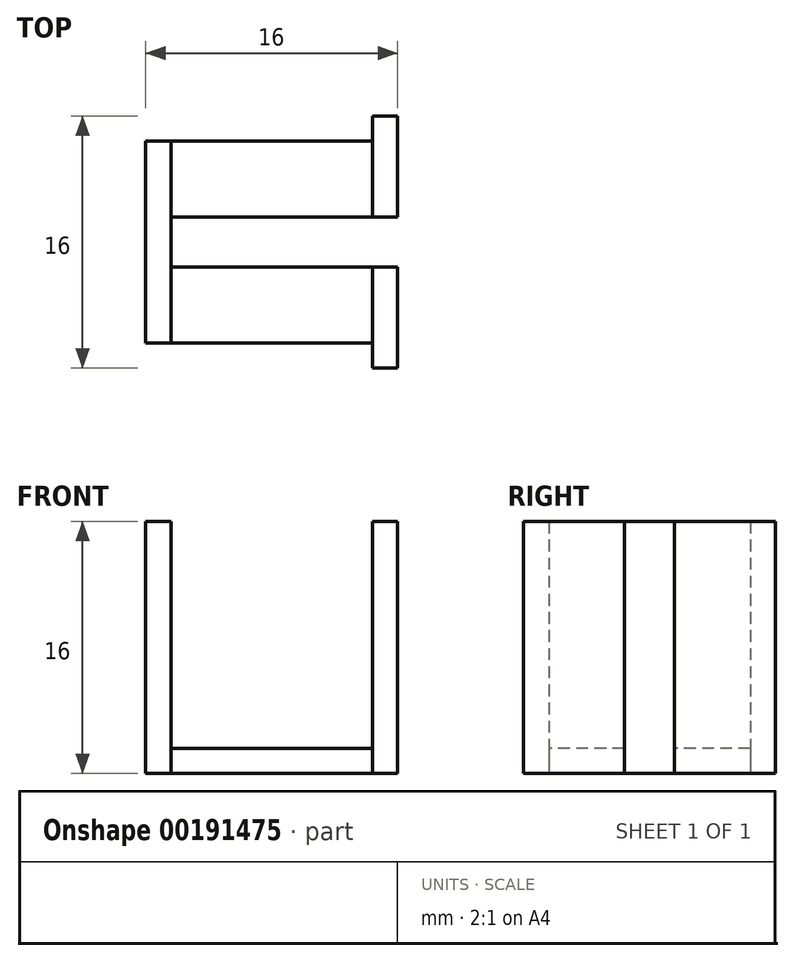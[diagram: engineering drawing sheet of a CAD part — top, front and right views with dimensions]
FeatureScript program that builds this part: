
annotation { "Feature Type Name" : "Feature", "Feature Type Description" : "" }
export const myFeature = defineFeature(function(context is Context, id is Id, definition is map)
    precondition{}
    {
        {
            assignVariable(context, id + "F0", {"name" : "FLU", "anyValue" : 1.6});
        }
        {
            var Q0;
            Q0=qCreatedBy(makeId("Top.planeOp"),FACE);
            var sketch = newSketch(context, id + "F1", { "sketchPlane" : qUnion([Q0])});
            skLineSegment(sketch, "E0.bottom", {"start": v(8, 8) * mm, "end": v(-8, 8) * mm});
            skLineSegment(sketch, "E0.top", {"start": v(8, -8) * mm, "end": v(-8, -8) * mm});
            skLineSegment(sketch, "E0.left", {"start": v(8, 8) * mm, "end": v(8, -8) * mm});
            skLineSegment(sketch, "E0.right", {"start": v(-8, 8) * mm, "end": v(-8, -8) * mm});
            skPoint(sketch, "E0.middle", {"position": v(0, 0) * mm});
            skLineSegment(sketch, "E1", {"start": v(-6.4, 8) * mm, "end": v(-6.4, -8) * mm});
            skLineSegment(sketch, "E2", {"start": v(6.4, 8) * mm, "end": v(6.4, -8) * mm});
            skLineSegment(sketch, "E3", {"start": v(-8, 6.4) * mm, "end": v(8, 6.4) * mm});
            skLineSegment(sketch, "E4", {"start": v(-8, -6.4) * mm, "end": v(8.33, -6.4) * mm});
            skLineSegment(sketch, "E5", {"start": v(-8, 1.6) * mm, "end": v(8, 1.6) * mm});
            skLineSegment(sketch, "E6", {"start": v(-8, -1.6) * mm, "end": v(8, -1.6) * mm});
            skSolve(sketch);
        }
        {
            var Q0;
            {var subQ0=sQuery(id+"F1.wireOp",EDGE,"E0.left");var subQ1=sQuery(id+"F1.wireOp",EDGE,"E0.top");var subQ2=makeQuery(id+"F1.imprint","INTERSECT",VERTEX,{"derivedFrom":[subQ1,subQ0]});Q0=makeQuery(id+"F1.imprint","IMPRINT",FACE,{"disambiguationData":[TD([[makeQuery(id+"F1.imprint","IMPRINT",EDGE,{"disambiguationData":[TD([[subQ2,-1.0]])],"derivedFrom":subQ1}),-1.0]])]});}
            var Q1;
            {var subQ0=sQuery(id+"F1.wireOp",EDGE,"E6");var subQ1=sQuery(id+"F1.wireOp",EDGE,"E0.left");var subQ2=makeQuery(id+"F1.imprint","INTERSECT",VERTEX,{"derivedFrom":[subQ1,subQ0]});Q1=makeQuery(id+"F1.imprint","IMPRINT",FACE,{"disambiguationData":[TD([[makeQuery(id+"F1.imprint","IMPRINT",EDGE,{"disambiguationData":[TD([[subQ2,-1.0]])],"derivedFrom":subQ1}),-1.0]])]});}
            var Q2;
            {var subQ0=sQuery(id+"F1.wireOp",EDGE,"E4");var subQ1=sQuery(id+"F1.wireOp",EDGE,"E0.right");var subQ2=makeQuery(id+"F1.imprint","INTERSECT",VERTEX,{"derivedFrom":[subQ1,subQ0]});Q2=makeQuery(id+"F1.imprint","IMPRINT",FACE,{"disambiguationData":[TD([[makeQuery(id+"F1.imprint","IMPRINT",EDGE,{"disambiguationData":[TD([[subQ2,1.0]])],"derivedFrom":subQ1}),1.0]])]});}
            var Q3;
            {var subQ0=sQuery(id+"F1.wireOp",EDGE,"E5");var subQ1=sQuery(id+"F1.wireOp",EDGE,"E0.right");var subQ2=makeQuery(id+"F1.imprint","INTERSECT",VERTEX,{"derivedFrom":[subQ1,subQ0]});Q3=makeQuery(id+"F1.imprint","IMPRINT",FACE,{"disambiguationData":[TD([[makeQuery(id+"F1.imprint","IMPRINT",EDGE,{"disambiguationData":[TD([[subQ2,-1.0]])],"derivedFrom":subQ1}),1.0]])]});}
            var Q4;
            {var subQ0=sQuery(id+"F1.wireOp",EDGE,"E3");var subQ1=sQuery(id+"F1.wireOp",EDGE,"E0.right");var subQ2=makeQuery(id+"F1.imprint","INTERSECT",VERTEX,{"derivedFrom":[subQ1,subQ0]});Q4=makeQuery(id+"F1.imprint","IMPRINT",FACE,{"disambiguationData":[TD([[makeQuery(id+"F1.imprint","IMPRINT",EDGE,{"disambiguationData":[TD([[subQ2,-1.0]])],"derivedFrom":subQ1}),1.0]])]});}
            var Q5;
            {var subQ0=sQuery(id+"F1.wireOp",EDGE,"E3");var subQ1=sQuery(id+"F1.wireOp",EDGE,"E0.left");var subQ2=makeQuery(id+"F1.imprint","INTERSECT",VERTEX,{"derivedFrom":[subQ1,subQ0]});Q5=makeQuery(id+"F1.imprint","IMPRINT",FACE,{"disambiguationData":[TD([[makeQuery(id+"F1.imprint","IMPRINT",EDGE,{"disambiguationData":[TD([[subQ2,-1.0]])],"derivedFrom":subQ1}),-1.0]])]});}
            var Q6;
            {var subQ0=sQuery(id+"F1.wireOp",EDGE,"E0.left");var subQ1=sQuery(id+"F1.wireOp",EDGE,"E0.bottom");var subQ2=makeQuery(id+"F1.imprint","INTERSECT",VERTEX,{"derivedFrom":[subQ1,subQ0]});Q6=makeQuery(id+"F1.imprint","IMPRINT",FACE,{"disambiguationData":[TD([[makeQuery(id+"F1.imprint","IMPRINT",EDGE,{"disambiguationData":[TD([[subQ2,-1.0]])],"derivedFrom":subQ1}),1.0]])]});}
            extrude(context, id + "F2", {"entities" : qUnion([Q0, Q1, Q2, Q3, Q4, Q5, Q6]), "depth" : (10 * getVariable(context, 'FLU')) * mm});
        }
        {
            var Q0;
            {var subQ0=sQuery(id+"F1.wireOp",EDGE,"E3");var subQ1=sQuery(id+"F1.wireOp",EDGE,"E1");var subQ2=makeQuery(id+"F1.imprint","INTERSECT",VERTEX,{"derivedFrom":[subQ1,subQ0]});Q0=makeQuery(id+"F1.imprint","IMPRINT",FACE,{"disambiguationData":[TD([[makeQuery(id+"F1.imprint","IMPRINT",EDGE,{"disambiguationData":[TD([[subQ2,-1.0]])],"derivedFrom":subQ1}),1.0]])]});}
            var Q1;
            {var subQ0=sQuery(id+"F1.wireOp",EDGE,"E6");var subQ1=sQuery(id+"F1.wireOp",EDGE,"E1");var subQ2=makeQuery(id+"F1.imprint","INTERSECT",VERTEX,{"derivedFrom":[subQ1,subQ0]});Q1=makeQuery(id+"F1.imprint","IMPRINT",FACE,{"disambiguationData":[TD([[makeQuery(id+"F1.imprint","IMPRINT",EDGE,{"disambiguationData":[TD([[subQ2,-1.0]])],"derivedFrom":subQ1}),1.0]])]});}
            extrude(context, id + "F3", {"entities" : qUnion([Q0, Q1]), "depth" : (getVariable(context, 'FLU')) * mm});
        }
    });
